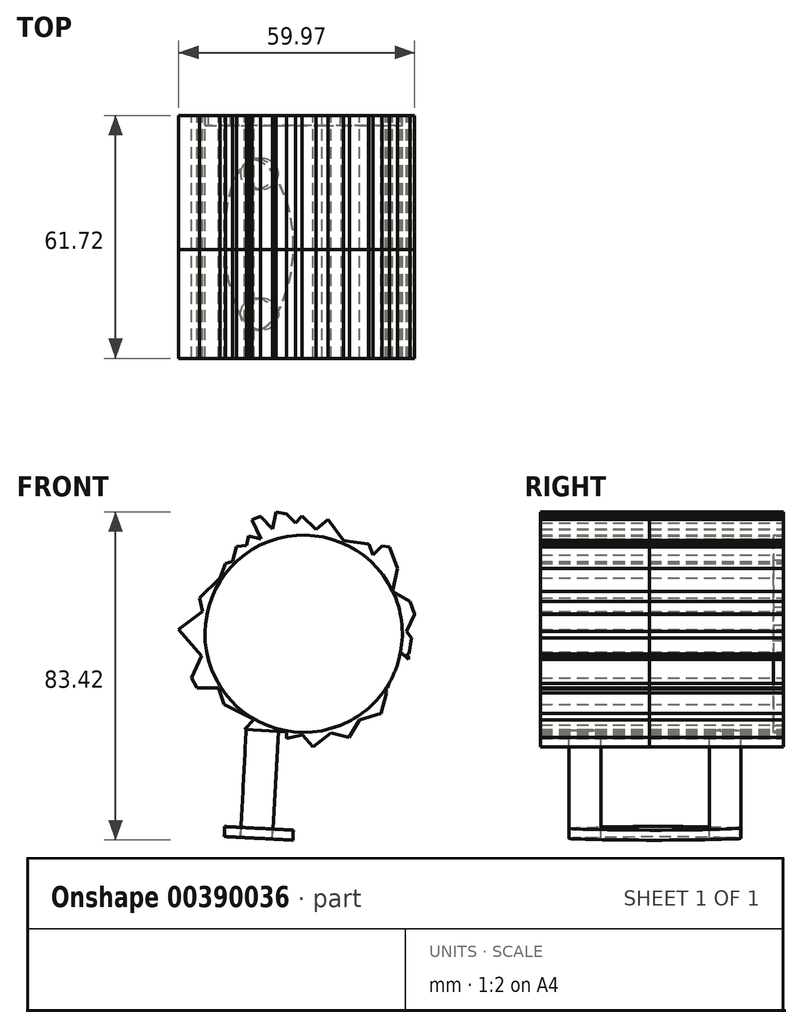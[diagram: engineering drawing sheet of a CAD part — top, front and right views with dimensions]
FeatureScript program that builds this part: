
annotation { "Feature Type Name" : "Feature", "Feature Type Description" : "" }
export const myFeature = defineFeature(function(context is Context, id is Id, definition is map)
    precondition{}
    {
        {
            var Q0;
            Q0=qCreatedBy(makeId("Front.planeOp"),FACE);
            var sketch = newSketch(context, id + "F0", { "sketchPlane" : qUnion([Q0])});
            skCircle(sketch, "E0", {"center": v(0, 0) * mm, "radius": 31.78 * mm});
            skCircle(sketch, "E1", {"center": v(0, 0) * mm, "radius": 25.06 * mm});
            skLineSegment(sketch, "E2", {"start": v(28.67, -13.71) * mm, "end": v(22.7, -10.64) * mm});
            skLineSegment(sketch, "E3", {"start": v(22.7, -10.64) * mm, "end": v(28.67, -13.71) * mm});
            skLineSegment(sketch, "E4", {"start": v(24.63, -4.65) * mm, "end": v(31.2, -6.06) * mm});
            skLineSegment(sketch, "E5", {"start": v(31.2, -6.06) * mm, "end": v(24.98, 2.05) * mm});
            skLineSegment(sketch, "E6", {"start": v(24.98, 2.05) * mm, "end": v(31.27, 5.68) * mm});
            skLineSegment(sketch, "E7", {"start": v(31.27, 5.68) * mm, "end": v(22.62, 10.8) * mm});
            skLineSegment(sketch, "E8", {"start": v(22.62, 10.8) * mm, "end": v(24.6, 20.1) * mm});
            skLineSegment(sketch, "E9", {"start": v(24.6, 20.1) * mm, "end": v(31.56, -3.73) * mm});
            skLineSegment(sketch, "E10", {"start": v(31.56, -3.73) * mm, "end": v(21.15, 23.72) * mm});
            skLineSegment(sketch, "E11", {"start": v(21.15, 23.72) * mm, "end": v(16.52, 18.85) * mm});
            skLineSegment(sketch, "E12", {"start": v(16.52, 18.85) * mm, "end": v(16.52, 27.15) * mm});
            skLineSegment(sketch, "E13", {"start": v(16.52, 27.15) * mm, "end": v(12.53, 21.7) * mm});
            skLineSegment(sketch, "E14", {"start": v(12.53, 21.7) * mm, "end": v(21.15, 23.72) * mm});
            skLineSegment(sketch, "E15", {"start": v(12.53, 21.7) * mm, "end": v(8.2, 30.7) * mm});
            skLineSegment(sketch, "E16", {"start": v(8.2, 30.7) * mm, "end": v(1.3, 25.03) * mm});
            skLineSegment(sketch, "E17", {"start": v(1.3, 25.03) * mm, "end": v(-4.38, 30.44) * mm});
            skLineSegment(sketch, "E18", {"start": v(-4.38, 30.44) * mm, "end": v(-5.66, 24.42) * mm});
            skLineSegment(sketch, "E19", {"start": v(-5.66, 24.42) * mm, "end": v(1.32, 31.75) * mm});
            skLineSegment(sketch, "E20", {"start": v(1.32, 31.75) * mm, "end": v(-4.38, 30.44) * mm});
            skLineSegment(sketch, "E21", {"start": v(-4.38, 30.44) * mm, "end": v(-7, 31) * mm});
            skLineSegment(sketch, "E22", {"start": v(-7, 31) * mm, "end": v(-8.58, 23.55) * mm});
            skLineSegment(sketch, "E23", {"start": v(-8.58, 23.55) * mm, "end": v(-18.38, 25.93) * mm});
            skLineSegment(sketch, "E24", {"start": v(-18.38, 25.93) * mm, "end": v(-15, 20.08) * mm});
            skLineSegment(sketch, "E25", {"start": v(-15, 20.08) * mm, "end": v(-13.1, 28.95) * mm});
            skLineSegment(sketch, "E26", {"start": v(-13.1, 28.95) * mm, "end": v(-10.3, 22.85) * mm});
            skLineSegment(sketch, "E27", {"start": v(-10.3, 22.85) * mm, "end": v(-23.2, 21.7) * mm});
            skLineSegment(sketch, "E28", {"start": v(-23.2, 21.7) * mm, "end": v(-18.34, 17.08) * mm});
            skLineSegment(sketch, "E29", {"start": v(-18.34, 17.08) * mm, "end": v(-15.8, 27.57) * mm});
            skLineSegment(sketch, "E30", {"start": v(-15.8, 27.57) * mm, "end": v(-23.2, 9.5) * mm});
            skLineSegment(sketch, "E31", {"start": v(-23.2, 9.5) * mm, "end": v(-26.44, 17.63) * mm});
            skLineSegment(sketch, "E32", {"start": v(-26.44, 17.63) * mm, "end": v(-20.07, 15.02) * mm});
            skLineSegment(sketch, "E33", {"start": v(-20.07, 15.02) * mm, "end": v(-29.9, 10.78) * mm});
            skLineSegment(sketch, "E34", {"start": v(-29.9, 10.78) * mm, "end": v(-24.96, 2.24) * mm});
            skLineSegment(sketch, "E35", {"start": v(-24.96, 2.24) * mm, "end": v(-27.74, 15.5) * mm});
            skLineSegment(sketch, "E36", {"start": v(-27.74, 15.5) * mm, "end": v(-16.65, 18.74) * mm});
            skLineSegment(sketch, "E37", {"start": v(-16.65, 18.74) * mm, "end": v(-31.52, 4.06) * mm});
            skLineSegment(sketch, "E38", {"start": v(-31.52, 4.06) * mm, "end": v(-25.05, -0.69) * mm});
            skLineSegment(sketch, "E39", {"start": v(-25.05, -0.69) * mm, "end": v(-31.58, -3.5) * mm});
            skLineSegment(sketch, "E40", {"start": v(-31.58, -3.5) * mm, "end": v(-23.73, -8.07) * mm});
            skLineSegment(sketch, "E41", {"start": v(-23.73, -8.07) * mm, "end": v(-31.76, 1.15) * mm});
            skLineSegment(sketch, "E42", {"start": v(-31.76, 1.15) * mm, "end": v(-24.13, 6.78) * mm});
            skLineSegment(sketch, "E43", {"start": v(-24.13, 6.78) * mm, "end": v(-24.96, 2.24) * mm});
            skLineSegment(sketch, "E44", {"start": v(-24.84, -3.3) * mm, "end": v(-29.17, -12.6) * mm});
            skLineSegment(sketch, "E45", {"start": v(-29.17, -12.6) * mm, "end": v(-22.66, -10.7) * mm});
            skLineSegment(sketch, "E46", {"start": v(-22.66, -10.7) * mm, "end": v(-31.1, -6.5) * mm});
            skLineSegment(sketch, "E47", {"start": v(-31.1, -6.5) * mm, "end": v(-21.95, -22.98) * mm});
            skLineSegment(sketch, "E48", {"start": v(-21.95, -22.98) * mm, "end": v(-20.98, -13.71) * mm});
            skLineSegment(sketch, "E49", {"start": v(-20.98, -13.71) * mm, "end": v(-28.67, -13.71) * mm});
            skLineSegment(sketch, "E50", {"start": v(-28.67, -13.71) * mm, "end": v(-12.57, -21.74) * mm});
            skLineSegment(sketch, "E51", {"start": v(-12.57, -21.74) * mm, "end": v(-17.27, -26.67) * mm});
            skLineSegment(sketch, "E52", {"start": v(-17.27, -26.67) * mm, "end": v(-22.66, -10.7) * mm});
            skLineSegment(sketch, "E53", {"start": v(-22.66, -10.7) * mm, "end": v(-20.83, -24) * mm});
            skLineSegment(sketch, "E54", {"start": v(-20.83, -24) * mm, "end": v(-4.38, -24.87) * mm});
            skLineSegment(sketch, "E55", {"start": v(-4.38, -24.87) * mm, "end": v(-4.38, -31.47) * mm});
            skLineSegment(sketch, "E56", {"start": v(-4.38, -31.47) * mm, "end": v(-10.3, -22.85) * mm});
            skLineSegment(sketch, "E57", {"start": v(-10.3, -22.85) * mm, "end": v(-13.69, -28.68) * mm});
            skLineSegment(sketch, "E58", {"start": v(-13.69, -28.68) * mm, "end": v(4.1, -24.73) * mm});
            skLineSegment(sketch, "E59", {"start": v(4.1, -24.73) * mm, "end": v(4.74, -31.42) * mm});
            skLineSegment(sketch, "E60", {"start": v(4.74, -31.42) * mm, "end": v(-0.8, -25.05) * mm});
            skLineSegment(sketch, "E61", {"start": v(-0.8, -25.05) * mm, "end": v(-1.35, -31.75) * mm});
            skLineSegment(sketch, "E62", {"start": v(-1.35, -31.75) * mm, "end": v(9.56, -23.17) * mm});
            skLineSegment(sketch, "E63", {"start": v(9.56, -23.17) * mm, "end": v(21.75, -23.17) * mm});
            skLineSegment(sketch, "E64", {"start": v(21.75, -23.17) * mm, "end": v(9.17, -30.42) * mm});
            skLineSegment(sketch, "E65", {"start": v(9.17, -30.42) * mm, "end": v(15.34, -19.82) * mm});
            skLineSegment(sketch, "E66", {"start": v(15.34, -19.82) * mm, "end": v(16.07, -27.41) * mm});
            skLineSegment(sketch, "E67", {"start": v(16.07, -27.41) * mm, "end": v(4.62, -24.63) * mm});
            skLineSegment(sketch, "E68", {"start": v(4.62, -24.63) * mm, "end": v(25.88, -18.44) * mm});
            skLineSegment(sketch, "E69", {"start": v(25.88, -18.44) * mm, "end": v(24.63, -4.65) * mm});
            skLineSegment(sketch, "E70", {"start": v(24.63, -4.65) * mm, "end": v(30.18, -9.94) * mm});
            skLineSegment(sketch, "E71", {"start": v(30.18, -9.94) * mm, "end": v(20.8, -13.98) * mm});
            skLineSegment(sketch, "E72", {"start": v(20.8, -13.98) * mm, "end": v(22.7, -22.24) * mm});
            skLineSegment(sketch, "E73", {"start": v(22.7, -22.24) * mm, "end": v(17.22, -18.21) * mm});
            skLineSegment(sketch, "E74", {"start": v(17.22, -18.21) * mm, "end": v(17.99, -26.2) * mm});
            skLineSegment(sketch, "E75", {"start": v(17.99, -26.2) * mm, "end": v(21.66, -12.6) * mm});
            skLineSegment(sketch, "E76", {"start": v(21.66, -12.6) * mm, "end": v(24.8, -19.88) * mm});
            skLineSegment(sketch, "E77", {"start": v(24.8, -19.88) * mm, "end": v(29.22, 12.48) * mm});
            skLineSegment(sketch, "E78", {"start": v(29.22, 12.48) * mm, "end": v(31.56, -4.65) * mm});
            skLineSegment(sketch, "E79", {"start": v(31.56, -4.65) * mm, "end": v(29.17, -12.6) * mm});
            skLineSegment(sketch, "E80", {"start": v(29.17, -12.6) * mm, "end": v(24.98, -1.56) * mm});
            skLineSegment(sketch, "E81", {"start": v(24.98, -1.56) * mm, "end": v(30.18, 8.9) * mm});
            skLineSegment(sketch, "E82", {"start": v(30.18, 8.9) * mm, "end": v(24.17, 6.62) * mm});
            skLineSegment(sketch, "E83", {"start": v(24.17, 6.62) * mm, "end": v(26.74, 17.18) * mm});
            skLineSegment(sketch, "E84", {"start": v(26.74, 17.18) * mm, "end": v(18.93, 16.43) * mm});
            skLineSegment(sketch, "E85", {"start": v(18.93, 16.43) * mm, "end": v(22.98, 21.95) * mm});
            skLineSegment(sketch, "E86", {"start": v(22.98, 21.95) * mm, "end": v(6.53, 24.2) * mm});
            skLineSegment(sketch, "E87", {"start": v(6.53, 24.2) * mm, "end": v(12.36, 29.28) * mm});
            skLineSegment(sketch, "E88", {"start": v(12.36, 29.28) * mm, "end": v(-0.35, 30) * mm});
            skLineSegment(sketch, "E89", {"start": v(-0.35, 30) * mm, "end": v(5.02, 24.56) * mm});
            skLineSegment(sketch, "E90", {"start": v(5.02, 24.56) * mm, "end": v(4.3, 31.49) * mm});
            skLineSegment(sketch, "E91", {"start": v(4.3, 31.49) * mm, "end": v(11.09, 22.48) * mm});
            skLineSegment(sketch, "E92", {"start": v(11.09, 22.48) * mm, "end": v(14.54, 28.26) * mm});
            skLineSegment(sketch, "E93", {"start": v(14.54, 28.26) * mm, "end": v(18.93, 16.43) * mm});
            skLineSegment(sketch, "E94", {"start": v(-11, 29.82) * mm, "end": v(-5.66, 24.42) * mm});
            skSolve(sketch);
        }
        {
            var Q0;
            {var subQ0=sQuery(id+"F0.wireOp",EDGE,"E94");var subQ3=sQuery(id+"F0.wireOp",EDGE,"E22");var subQ5=makeQuery(id+"F0.imprint","INTERSECT",VERTEX,{"derivedFrom":[subQ3,subQ0]});Q0=makeQuery(id+"F0.imprint","IMPRINT",FACE,{"disambiguationData":[TD([[makeQuery(id+"F0.imprint","IMPRINT",EDGE,{"disambiguationData":[TD([[subQ5,-1.0]])],"derivedFrom":subQ3}),1.0]])]});}
            var Q1;
            {var subQ0=sQuery(id+"F0.wireOp",EDGE,"E17");var subQ3=sQuery(id+"F0.wireOp",EDGE,"E19");var subQ5=makeQuery(id+"F0.imprint","INTERSECT",VERTEX,{"derivedFrom":[subQ0,subQ3]});Q1=makeQuery(id+"F0.imprint","IMPRINT",FACE,{"disambiguationData":[TD([[makeQuery(id+"F0.imprint","IMPRINT",EDGE,{"disambiguationData":[TD([[subQ5,1.0]])],"derivedFrom":subQ0}),1.0]])]});}
            var Q2;
            {var subQ0=sQuery(id+"F0.wireOp",EDGE,"E16");var subQ3=sQuery(id+"F0.wireOp",EDGE,"E89");var subQ5=makeQuery(id+"F0.imprint","INTERSECT",VERTEX,{"derivedFrom":[subQ0,subQ3]});Q2=makeQuery(id+"F0.imprint","IMPRINT",FACE,{"disambiguationData":[TD([[makeQuery(id+"F0.imprint","IMPRINT",EDGE,{"disambiguationData":[TD([[subQ5,-1.0]])],"derivedFrom":subQ0}),1.0]])]});}
            var Q3;
            {var subQ0=sQuery(id+"F0.wireOp",EDGE,"E86");var subQ3=sQuery(id+"F0.wireOp",EDGE,"E91");var subQ5=makeQuery(id+"F0.imprint","INTERSECT",VERTEX,{"derivedFrom":[subQ0,subQ3]});Q3=makeQuery(id+"F0.imprint","IMPRINT",FACE,{"disambiguationData":[TD([[makeQuery(id+"F0.imprint","IMPRINT",EDGE,{"disambiguationData":[TD([[subQ5,-1.0]])],"derivedFrom":subQ0}),1.0]])]});}
            var Q4;
            {var subQ3=sQuery(id+"F0.wireOp",EDGE,"E16");var subQ7=sQuery(id+"F0.wireOp",EDGE,"E91");var subQ9=makeQuery(id+"F0.imprint","INTERSECT",VERTEX,{"derivedFrom":[subQ3,subQ7]});Q4=makeQuery(id+"F0.imprint","IMPRINT",FACE,{"disambiguationData":[TD([[makeQuery(id+"F0.imprint","IMPRINT",EDGE,{"disambiguationData":[TD([[subQ9,-1.0]])],"derivedFrom":subQ3}),1.0]])]});}
            var Q5;
            {var subQ0=sQuery(id+"F0.wireOp",EDGE,"E15");var subQ3=sQuery(id+"F0.wireOp",EDGE,"E92");var subQ5=makeQuery(id+"F0.imprint","INTERSECT",VERTEX,{"derivedFrom":[subQ0,subQ3]});Q5=makeQuery(id+"F0.imprint","IMPRINT",FACE,{"disambiguationData":[TD([[makeQuery(id+"F0.imprint","IMPRINT",EDGE,{"disambiguationData":[TD([[subQ5,1.0]])],"derivedFrom":subQ3}),-1.0]])]});}
            var Q6;
            {var subQ0=sQuery(id+"F0.wireOp",EDGE,"E92");var subQ1=sQuery(id+"F0.wireOp",EDGE,"E15");var subQ2=makeQuery(id+"F0.imprint","INTERSECT",VERTEX,{"derivedFrom":[subQ1,subQ0]});Q6=makeQuery(id+"F0.imprint","IMPRINT",FACE,{"disambiguationData":[TD([[makeQuery(id+"F0.imprint","IMPRINT",EDGE,{"disambiguationData":[TD([[subQ2,-1.0]])],"derivedFrom":subQ1}),1.0]])]});}
            var Q7;
            {var subQ0=sQuery(id+"F0.wireOp",EDGE,"E12");var subQ3=sQuery(id+"F0.wireOp",EDGE,"E14");var subQ5=makeQuery(id+"F0.imprint","INTERSECT",VERTEX,{"derivedFrom":[subQ0,subQ3]});Q7=makeQuery(id+"F0.imprint","IMPRINT",FACE,{"disambiguationData":[TD([[makeQuery(id+"F0.imprint","IMPRINT",EDGE,{"disambiguationData":[TD([[subQ5,1.0]])],"derivedFrom":subQ0}),1.0]])]});}
            var Q8;
            {var subQ0=sQuery(id+"F0.wireOp",EDGE,"E11");var subQ3=sQuery(id+"F0.wireOp",EDGE,"E93");var subQ5=makeQuery(id+"F0.imprint","INTERSECT",VERTEX,{"derivedFrom":[subQ0,subQ3]});Q8=makeQuery(id+"F0.imprint","IMPRINT",FACE,{"disambiguationData":[TD([[makeQuery(id+"F0.imprint","IMPRINT",EDGE,{"disambiguationData":[TD([[subQ5,-1.0]])],"derivedFrom":subQ0}),1.0]])]});}
            var Q9;
            {var subQ0=sQuery(id+"F0.wireOp",EDGE,"E8");var subQ5=sQuery(id+"F0.wireOp",EDGE,"E10");var subQ6=makeQuery(id+"F0.imprint","INTERSECT",VERTEX,{"derivedFrom":[subQ0,subQ5]});Q9=makeQuery(id+"F0.imprint","IMPRINT",FACE,{"disambiguationData":[TD([[makeQuery(id+"F0.imprint","IMPRINT",EDGE,{"disambiguationData":[TD([[subQ6,-1.0]])],"derivedFrom":subQ5}),1.0]])]});}
            var Q10;
            {var subQ0=sQuery(id+"F0.wireOp",EDGE,"E7");var subQ3=sQuery(id+"F0.wireOp",EDGE,"E83");var subQ5=makeQuery(id+"F0.imprint","INTERSECT",VERTEX,{"derivedFrom":[subQ0,subQ3]});Q10=makeQuery(id+"F0.imprint","IMPRINT",FACE,{"disambiguationData":[TD([[makeQuery(id+"F0.imprint","IMPRINT",EDGE,{"disambiguationData":[TD([[subQ5,-1.0]])],"derivedFrom":subQ0}),1.0]])]});}
            var Q11;
            {var subQ0=sQuery(id+"F0.wireOp",EDGE,"E77");var subQ1=sQuery(id+"F0.wireOp",EDGE,"E10");var subQ2=makeQuery(id+"F0.imprint","INTERSECT",VERTEX,{"derivedFrom":[subQ1,subQ0]});Q11=makeQuery(id+"F0.imprint","IMPRINT",FACE,{"disambiguationData":[TD([[makeQuery(id+"F0.imprint","IMPRINT",EDGE,{"disambiguationData":[TD([[subQ2,-1.0]])],"derivedFrom":subQ1}),1.0]])]});}
            var Q12;
            {var subQ1=sQuery(id+"F0.wireOp",EDGE,"E1");var subQ3=sQuery(id+"F0.wireOp",EDGE,"E81");var subQ4=makeQuery(id+"F0.imprint","INTERSECT",VERTEX,{"derivedFrom":[subQ1,subQ3]});Q12=makeQuery(id+"F0.imprint","IMPRINT",FACE,{"disambiguationData":[TD([[makeQuery(id+"F0.imprint","IMPRINT",EDGE,{"disambiguationData":[TD([[subQ4,-1.0]])],"derivedFrom":subQ3}),1.0]])]});}
            var Q13;
            {var subQ1=sQuery(id+"F0.wireOp",EDGE,"E1");var subQ3=sQuery(id+"F0.wireOp",EDGE,"E80");var subQ4=makeQuery(id+"F0.imprint","INTERSECT",VERTEX,{"derivedFrom":[subQ1,subQ3]});Q13=makeQuery(id+"F0.imprint","IMPRINT",FACE,{"disambiguationData":[TD([[makeQuery(id+"F0.imprint","IMPRINT",EDGE,{"disambiguationData":[TD([[subQ4,1.0]])],"derivedFrom":subQ3}),1.0]])]});}
            var Q14;
            {var subQ0=sQuery(id+"F0.wireOp",EDGE,"E3");var subQ1=sQuery(id+"F0.wireOp",EDGE,"E1");var subQ2=makeQuery(id+"F0.imprint","INTERSECT",VERTEX,{"derivedFrom":[subQ1,subQ0]});Q14=makeQuery(id+"F0.imprint","IMPRINT",FACE,{"disambiguationData":[TD([[makeQuery(id+"F0.imprint","IMPRINT",EDGE,{"disambiguationData":[TD([[subQ2,-1.0]])],"derivedFrom":subQ0}),1.0]])]});}
            var Q15;
            {var subQ0=sQuery(id+"F0.wireOp",EDGE,"E71");var subQ3=sQuery(id+"F0.wireOp",EDGE,"E75");var subQ5=makeQuery(id+"F0.imprint","INTERSECT",VERTEX,{"derivedFrom":[subQ0,subQ3]});Q15=makeQuery(id+"F0.imprint","IMPRINT",FACE,{"disambiguationData":[TD([[makeQuery(id+"F0.imprint","IMPRINT",EDGE,{"disambiguationData":[TD([[subQ5,-1.0]])],"derivedFrom":subQ0}),-1.0]])]});}
            var Q16;
            {var subQ0=sQuery(id+"F0.wireOp",EDGE,"E72");var subQ5=sQuery(id+"F0.wireOp",EDGE,"E75");var subQ6=makeQuery(id+"F0.imprint","INTERSECT",VERTEX,{"derivedFrom":[subQ0,subQ5]});Q16=makeQuery(id+"F0.imprint","IMPRINT",FACE,{"disambiguationData":[TD([[makeQuery(id+"F0.imprint","IMPRINT",EDGE,{"disambiguationData":[TD([[subQ6,1.0]])],"derivedFrom":subQ5}),1.0]])]});}
            var Q17;
            {var subQ5=sQuery(id+"F0.wireOp",EDGE,"E3");var subQ7=sQuery(id+"F0.wireOp",EDGE,"E1");var subQ8=makeQuery(id+"F0.imprint","INTERSECT",VERTEX,{"derivedFrom":[subQ7,subQ5]});Q17=makeQuery(id+"F0.imprint","IMPRINT",FACE,{"disambiguationData":[TD([[makeQuery(id+"F0.imprint","IMPRINT",EDGE,{"disambiguationData":[TD([[subQ8,-1.0]])],"derivedFrom":subQ5}),-1.0]])]});}
            var Q18;
            {var subQ0=sQuery(id+"F0.wireOp",EDGE,"E66");var subQ5=sQuery(id+"F0.wireOp",EDGE,"E68");var subQ7=makeQuery(id+"F0.imprint","INTERSECT",VERTEX,{"derivedFrom":[subQ0,subQ5]});Q18=makeQuery(id+"F0.imprint","IMPRINT",FACE,{"disambiguationData":[TD([[makeQuery(id+"F0.imprint","IMPRINT",EDGE,{"disambiguationData":[TD([[subQ7,-1.0]])],"derivedFrom":subQ5}),1.0]])]});}
            var Q19;
            {var subQ0=sQuery(id+"F0.wireOp",EDGE,"E63");var subQ5=sQuery(id+"F0.wireOp",EDGE,"E68");var subQ6=makeQuery(id+"F0.imprint","INTERSECT",VERTEX,{"derivedFrom":[subQ0,subQ5]});Q19=makeQuery(id+"F0.imprint","IMPRINT",FACE,{"disambiguationData":[TD([[makeQuery(id+"F0.imprint","IMPRINT",EDGE,{"disambiguationData":[TD([[subQ6,-1.0]])],"derivedFrom":subQ5}),1.0]])]});}
            var Q20;
            {var subQ0=sQuery(id+"F0.wireOp",EDGE,"E58");var subQ3=sQuery(id+"F0.wireOp",EDGE,"E60");var subQ5=makeQuery(id+"F0.imprint","INTERSECT",VERTEX,{"derivedFrom":[subQ0,subQ3]});Q20=makeQuery(id+"F0.imprint","IMPRINT",FACE,{"disambiguationData":[TD([[makeQuery(id+"F0.imprint","IMPRINT",EDGE,{"disambiguationData":[TD([[subQ5,-1.0]])],"derivedFrom":subQ0}),1.0]])]});}
            var Q21;
            {var subQ3=sQuery(id+"F0.wireOp",EDGE,"E54");var subQ5=sQuery(id+"F0.wireOp",EDGE,"E55");var subQ6=makeQuery(id+"F0.imprint","INTERSECT",VERTEX,{"derivedFrom":[subQ3,subQ5]});Q21=makeQuery(id+"F0.imprint","IMPRINT",FACE,{"disambiguationData":[TD([[makeQuery(id+"F0.imprint","IMPRINT",EDGE,{"disambiguationData":[TD([[subQ6,1.0]])],"derivedFrom":subQ3}),1.0]])]});}
            var Q22;
            {var subQ0=sQuery(id+"F0.wireOp",EDGE,"E61");var subQ1=sQuery(id+"F0.wireOp",EDGE,"E58");var subQ2=makeQuery(id+"F0.imprint","INTERSECT",VERTEX,{"derivedFrom":[subQ1,subQ0]});Q22=makeQuery(id+"F0.imprint","IMPRINT",FACE,{"disambiguationData":[TD([[makeQuery(id+"F0.imprint","IMPRINT",EDGE,{"disambiguationData":[TD([[subQ2,-1.0]])],"derivedFrom":subQ1}),1.0]])]});}
            var Q23;
            {var subQ0=sQuery(id+"F0.wireOp",EDGE,"E51");var subQ1=sQuery(id+"F0.wireOp",EDGE,"E50");var subQ2=makeQuery(id+"F0.imprint","INTERSECT",VERTEX,{"derivedFrom":[subQ1,subQ0]});Q23=makeQuery(id+"F0.imprint","IMPRINT",FACE,{"disambiguationData":[TD([[makeQuery(id+"F0.imprint","IMPRINT",EDGE,{"disambiguationData":[TD([[subQ2,1.0]])],"derivedFrom":subQ1}),1.0]])]});}
            var Q24;
            {var subQ1=sQuery(id+"F0.wireOp",EDGE,"E48");var subQ3=sQuery(id+"F0.wireOp",EDGE,"E52");var subQ4=makeQuery(id+"F0.imprint","INTERSECT",VERTEX,{"derivedFrom":[subQ1,subQ3]});Q24=makeQuery(id+"F0.imprint","IMPRINT",FACE,{"disambiguationData":[TD([[makeQuery(id+"F0.imprint","IMPRINT",EDGE,{"disambiguationData":[TD([[subQ4,-1.0]])],"derivedFrom":subQ3}),-1.0]])]});}
            var Q25;
            {var subQ0=sQuery(id+"F0.wireOp",EDGE,"E52");var subQ3=sQuery(id+"F0.wireOp",EDGE,"E49");var subQ5=makeQuery(id+"F0.imprint","INTERSECT",VERTEX,{"derivedFrom":[subQ3,subQ0]});Q25=makeQuery(id+"F0.imprint","IMPRINT",FACE,{"disambiguationData":[TD([[makeQuery(id+"F0.imprint","IMPRINT",EDGE,{"disambiguationData":[TD([[subQ5,1.0]])],"derivedFrom":subQ3}),-1.0]])]});}
            var Q26;
            {var subQ0=sQuery(id+"F0.wireOp",EDGE,"E40");var subQ5=sQuery(id+"F0.wireOp",EDGE,"E44");var subQ6=makeQuery(id+"F0.imprint","INTERSECT",VERTEX,{"derivedFrom":[subQ0,subQ5]});Q26=makeQuery(id+"F0.imprint","IMPRINT",FACE,{"disambiguationData":[TD([[makeQuery(id+"F0.imprint","IMPRINT",EDGE,{"disambiguationData":[TD([[subQ6,-1.0]])],"derivedFrom":subQ5}),1.0]])]});}
            var Q27;
            {var subQ1=sQuery(id+"F0.wireOp",EDGE,"E1");var subQ3=sQuery(id+"F0.wireOp",EDGE,"E44");var subQ4=makeQuery(id+"F0.imprint","INTERSECT",VERTEX,{"derivedFrom":[subQ1,subQ3]});Q27=makeQuery(id+"F0.imprint","IMPRINT",FACE,{"disambiguationData":[TD([[makeQuery(id+"F0.imprint","IMPRINT",EDGE,{"disambiguationData":[TD([[subQ4,-1.0]])],"derivedFrom":subQ3}),1.0]])]});}
            var Q28;
            {var subQ1=sQuery(id+"F0.wireOp",EDGE,"E40");var subQ3=sQuery(id+"F0.wireOp",EDGE,"E44");var subQ4=makeQuery(id+"F0.imprint","INTERSECT",VERTEX,{"derivedFrom":[subQ1,subQ3]});Q28=makeQuery(id+"F0.imprint","IMPRINT",FACE,{"disambiguationData":[TD([[makeQuery(id+"F0.imprint","IMPRINT",EDGE,{"disambiguationData":[TD([[subQ4,1.0]])],"derivedFrom":subQ3}),1.0]])]});}
            var Q29;
            {var subQ0=sQuery(id+"F0.wireOp",EDGE,"E39");var subQ5=sQuery(id+"F0.wireOp",EDGE,"E41");var subQ6=makeQuery(id+"F0.imprint","INTERSECT",VERTEX,{"derivedFrom":[subQ0,subQ5]});Q29=makeQuery(id+"F0.imprint","IMPRINT",FACE,{"disambiguationData":[TD([[makeQuery(id+"F0.imprint","IMPRINT",EDGE,{"disambiguationData":[TD([[subQ6,1.0]])],"derivedFrom":subQ5}),-1.0]])]});}
            var Q30;
            {var subQ0=sQuery(id+"F0.wireOp",EDGE,"E34");var subQ5=sQuery(id+"F0.wireOp",EDGE,"E42");var subQ6=makeQuery(id+"F0.imprint","INTERSECT",VERTEX,{"derivedFrom":[subQ0,subQ5]});Q30=makeQuery(id+"F0.imprint","IMPRINT",FACE,{"disambiguationData":[TD([[makeQuery(id+"F0.imprint","IMPRINT",EDGE,{"disambiguationData":[TD([[subQ6,1.0]])],"derivedFrom":subQ5}),-1.0]])]});}
            var Q31;
            {var subQ1=sQuery(id+"F0.wireOp",EDGE,"E35");var subQ4=sQuery(id+"F0.wireOp",EDGE,"E42");var subQ6=makeQuery(id+"F0.imprint","INTERSECT",VERTEX,{"derivedFrom":[subQ1,subQ4]});Q31=makeQuery(id+"F0.imprint","IMPRINT",FACE,{"disambiguationData":[TD([[makeQuery(id+"F0.imprint","IMPRINT",EDGE,{"disambiguationData":[TD([[subQ6,-1.0]])],"derivedFrom":subQ4}),-1.0]])]});}
            var Q32;
            {var subQ3=sQuery(id+"F0.wireOp",EDGE,"E35");var subQ5=sQuery(id+"F0.wireOp",EDGE,"E42");var subQ6=makeQuery(id+"F0.imprint","INTERSECT",VERTEX,{"derivedFrom":[subQ3,subQ5]});Q32=makeQuery(id+"F0.imprint","IMPRINT",FACE,{"disambiguationData":[TD([[makeQuery(id+"F0.imprint","IMPRINT",EDGE,{"disambiguationData":[TD([[subQ6,-1.0]])],"derivedFrom":subQ3}),-1.0]])]});}
            var Q33;
            {var subQ1=sQuery(id+"F0.wireOp",EDGE,"E30");var subQ3=sQuery(id+"F0.wireOp",EDGE,"E37");var subQ4=makeQuery(id+"F0.imprint","INTERSECT",VERTEX,{"derivedFrom":[subQ1,subQ3]});Q33=makeQuery(id+"F0.imprint","IMPRINT",FACE,{"disambiguationData":[TD([[makeQuery(id+"F0.imprint","IMPRINT",EDGE,{"disambiguationData":[TD([[subQ4,-1.0]])],"derivedFrom":subQ3}),1.0]])]});}
            var Q34;
            {var subQ1=sQuery(id+"F0.wireOp",EDGE,"E32");var subQ3=sQuery(id+"F0.wireOp",EDGE,"E37");var subQ4=makeQuery(id+"F0.imprint","INTERSECT",VERTEX,{"derivedFrom":[subQ1,subQ3]});Q34=makeQuery(id+"F0.imprint","IMPRINT",FACE,{"disambiguationData":[TD([[makeQuery(id+"F0.imprint","IMPRINT",EDGE,{"disambiguationData":[TD([[subQ4,-1.0]])],"derivedFrom":subQ3}),1.0]])]});}
            var Q35;
            {var subQ1=sQuery(id+"F0.wireOp",EDGE,"E1");var subQ3=sQuery(id+"F0.wireOp",EDGE,"E37");var subQ4=makeQuery(id+"F0.imprint","INTERSECT",VERTEX,{"derivedFrom":[subQ1,subQ3]});Q35=makeQuery(id+"F0.imprint","IMPRINT",FACE,{"disambiguationData":[TD([[makeQuery(id+"F0.imprint","IMPRINT",EDGE,{"disambiguationData":[TD([[subQ4,-1.0]])],"derivedFrom":subQ3}),1.0]])]});}
            var Q36;
            {var subQ1=sQuery(id+"F0.wireOp",EDGE,"E30");var subQ5=sQuery(id+"F0.wireOp",EDGE,"E36");var subQ6=makeQuery(id+"F0.imprint","INTERSECT",VERTEX,{"derivedFrom":[subQ1,subQ5]});Q36=makeQuery(id+"F0.imprint","IMPRINT",FACE,{"disambiguationData":[TD([[makeQuery(id+"F0.imprint","IMPRINT",EDGE,{"disambiguationData":[TD([[subQ6,-1.0]])],"derivedFrom":subQ1}),1.0]])]});}
            var Q37;
            {var subQ0=sQuery(id+"F0.wireOp",EDGE,"E32");var subQ1=sQuery(id+"F0.wireOp",EDGE,"E30");var subQ2=makeQuery(id+"F0.imprint","INTERSECT",VERTEX,{"derivedFrom":[subQ1,subQ0]});Q37=makeQuery(id+"F0.imprint","IMPRINT",FACE,{"disambiguationData":[TD([[makeQuery(id+"F0.imprint","IMPRINT",EDGE,{"disambiguationData":[TD([[subQ2,-1.0]])],"derivedFrom":subQ1}),1.0]])]});}
            var Q38;
            {var subQ1=sQuery(id+"F0.wireOp",EDGE,"E28");var subQ3=sQuery(id+"F0.wireOp",EDGE,"E36");var subQ4=makeQuery(id+"F0.imprint","INTERSECT",VERTEX,{"derivedFrom":[subQ1,subQ3]});Q38=makeQuery(id+"F0.imprint","IMPRINT",FACE,{"disambiguationData":[TD([[makeQuery(id+"F0.imprint","IMPRINT",EDGE,{"disambiguationData":[TD([[subQ4,-1.0]])],"derivedFrom":subQ3}),-1.0]])]});}
            var Q39;
            {var subQ0=sQuery(id+"F0.wireOp",EDGE,"E33");var subQ1=sQuery(id+"F0.wireOp",EDGE,"E30");var subQ2=makeQuery(id+"F0.imprint","INTERSECT",VERTEX,{"derivedFrom":[subQ1,subQ0]});Q39=makeQuery(id+"F0.imprint","IMPRINT",FACE,{"disambiguationData":[TD([[makeQuery(id+"F0.imprint","IMPRINT",EDGE,{"disambiguationData":[TD([[subQ2,-1.0]])],"derivedFrom":subQ1}),1.0]])]});}
            var Q40;
            {var subQ0=sQuery(id+"F0.wireOp",EDGE,"E30");var subQ5=sQuery(id+"F0.wireOp",EDGE,"E37");var subQ6=makeQuery(id+"F0.imprint","INTERSECT",VERTEX,{"derivedFrom":[subQ0,subQ5]});Q40=makeQuery(id+"F0.imprint","IMPRINT",FACE,{"disambiguationData":[TD([[makeQuery(id+"F0.imprint","IMPRINT",EDGE,{"disambiguationData":[TD([[subQ6,1.0]])],"derivedFrom":subQ5}),1.0]])]});}
            var Q41;
            {var subQ0=sQuery(id+"F0.wireOp",EDGE,"E29");var subQ3=sQuery(id+"F0.wireOp",EDGE,"E36");var subQ5=makeQuery(id+"F0.imprint","INTERSECT",VERTEX,{"derivedFrom":[subQ0,subQ3]});Q41=makeQuery(id+"F0.imprint","IMPRINT",FACE,{"disambiguationData":[TD([[makeQuery(id+"F0.imprint","IMPRINT",EDGE,{"disambiguationData":[TD([[subQ5,1.0]])],"derivedFrom":subQ0}),-1.0]])]});}
            var Q42;
            {var subQ0=sQuery(id+"F0.wireOp",EDGE,"E27");var subQ1=sQuery(id+"F0.wireOp",EDGE,"E24");var subQ2=makeQuery(id+"F0.imprint","INTERSECT",VERTEX,{"derivedFrom":[subQ1,subQ0]});Q42=makeQuery(id+"F0.imprint","IMPRINT",FACE,{"disambiguationData":[TD([[makeQuery(id+"F0.imprint","IMPRINT",EDGE,{"disambiguationData":[TD([[subQ2,-1.0]])],"derivedFrom":subQ0}),1.0]])]});}
            var Q43;
            {var subQ0=sQuery(id+"F0.wireOp",EDGE,"E25");var subQ3=sQuery(id+"F0.wireOp",EDGE,"E27");var subQ5=makeQuery(id+"F0.imprint","INTERSECT",VERTEX,{"derivedFrom":[subQ0,subQ3]});Q43=makeQuery(id+"F0.imprint","IMPRINT",FACE,{"disambiguationData":[TD([[makeQuery(id+"F0.imprint","IMPRINT",EDGE,{"disambiguationData":[TD([[subQ5,1.0]])],"derivedFrom":subQ0}),-1.0]])]});}
            var Q44;
            {var subQ0=sQuery(id+"F0.wireOp",EDGE,"E23");var subQ3=sQuery(id+"F0.wireOp",EDGE,"E26");var subQ5=makeQuery(id+"F0.imprint","INTERSECT",VERTEX,{"derivedFrom":[subQ0,subQ3]});Q44=makeQuery(id+"F0.imprint","IMPRINT",FACE,{"disambiguationData":[TD([[makeQuery(id+"F0.imprint","IMPRINT",EDGE,{"disambiguationData":[TD([[subQ5,1.0]])],"derivedFrom":subQ0}),1.0]])]});}
            var Q45;
            {var subQ1=sQuery(id+"F0.wireOp",EDGE,"E24");var subQ3=sQuery(id+"F0.wireOp",EDGE,"E27");var subQ4=makeQuery(id+"F0.imprint","INTERSECT",VERTEX,{"derivedFrom":[subQ1,subQ3]});Q45=makeQuery(id+"F0.imprint","IMPRINT",FACE,{"disambiguationData":[TD([[makeQuery(id+"F0.imprint","IMPRINT",EDGE,{"disambiguationData":[TD([[subQ4,1.0]])],"derivedFrom":subQ3}),1.0]])]});}
            var Q46;
            {var subQ0=sQuery(id+"F0.wireOp",EDGE,"E26");var subQ1=sQuery(id+"F0.wireOp",EDGE,"E23");var subQ2=makeQuery(id+"F0.imprint","INTERSECT",VERTEX,{"derivedFrom":[subQ1,subQ0]});Q46=makeQuery(id+"F0.imprint","IMPRINT",FACE,{"disambiguationData":[TD([[makeQuery(id+"F0.imprint","IMPRINT",EDGE,{"disambiguationData":[TD([[subQ2,-1.0]])],"derivedFrom":subQ1}),1.0]])]});}
            var Q47;
            {var subQ0=sQuery(id+"F0.wireOp",EDGE,"E18");Q47=makeQuery(id+"F0.imprint","IMPRINT",FACE,{"disambiguationData":[TD([[makeQuery(id+"F0.imprint","IMPRINT",EDGE,{"derivedFrom":subQ0}),1.0]])]});}
            var Q48;
            {var subQ1=sQuery(id+"F0.wireOp",EDGE,"E86");var subQ3=sQuery(id+"F0.wireOp",EDGE,"E91");var subQ4=makeQuery(id+"F0.imprint","INTERSECT",VERTEX,{"derivedFrom":[subQ1,subQ3]});Q48=makeQuery(id+"F0.imprint","IMPRINT",FACE,{"disambiguationData":[TD([[makeQuery(id+"F0.imprint","IMPRINT",EDGE,{"disambiguationData":[TD([[subQ4,1.0]])],"derivedFrom":subQ3}),-1.0]])]});}
            var Q49;
            {var subQ0=sQuery(id+"F0.wireOp",EDGE,"E14");var subQ1=sQuery(id+"F0.wireOp",EDGE,"E12");var subQ2=makeQuery(id+"F0.imprint","INTERSECT",VERTEX,{"derivedFrom":[subQ1,subQ0]});Q49=makeQuery(id+"F0.imprint","IMPRINT",FACE,{"disambiguationData":[TD([[makeQuery(id+"F0.imprint","IMPRINT",EDGE,{"disambiguationData":[TD([[subQ2,-1.0]])],"derivedFrom":subQ1}),1.0]])]});}
            var Q50;
            {var subQ0=sQuery(id+"F0.wireOp",EDGE,"E12");var subQ5=sQuery(id+"F0.wireOp",EDGE,"E14");var subQ6=makeQuery(id+"F0.imprint","INTERSECT",VERTEX,{"derivedFrom":[subQ0,subQ5]});Q50=makeQuery(id+"F0.imprint","IMPRINT",FACE,{"disambiguationData":[TD([[makeQuery(id+"F0.imprint","IMPRINT",EDGE,{"disambiguationData":[TD([[subQ6,-1.0]])],"derivedFrom":subQ5}),-1.0]])]});}
            var Q51;
            {var subQ0=sQuery(id+"F0.wireOp",EDGE,"E84");var subQ1=sQuery(id+"F0.wireOp",EDGE,"E10");var subQ2=makeQuery(id+"F0.imprint","INTERSECT",VERTEX,{"derivedFrom":[subQ1,subQ0]});Q51=makeQuery(id+"F0.imprint","IMPRINT",FACE,{"disambiguationData":[TD([[makeQuery(id+"F0.imprint","IMPRINT",EDGE,{"disambiguationData":[TD([[subQ2,-1.0]])],"derivedFrom":subQ1}),1.0]])]});}
            var Q52;
            {var subQ0=sQuery(id+"F0.wireOp",EDGE,"E10");var subQ1=sQuery(id+"F0.wireOp",EDGE,"E7");var subQ2=makeQuery(id+"F0.imprint","INTERSECT",VERTEX,{"derivedFrom":[subQ1,subQ0]});Q52=makeQuery(id+"F0.imprint","IMPRINT",FACE,{"disambiguationData":[TD([[makeQuery(id+"F0.imprint","IMPRINT",EDGE,{"disambiguationData":[TD([[subQ2,-1.0]])],"derivedFrom":subQ1}),1.0]])]});}
            var Q53;
            {var subQ1=sQuery(id+"F0.wireOp",EDGE,"E5");var subQ3=sQuery(id+"F0.wireOp",EDGE,"E81");var subQ4=makeQuery(id+"F0.imprint","INTERSECT",VERTEX,{"derivedFrom":[subQ1,subQ3]});Q53=makeQuery(id+"F0.imprint","IMPRINT",FACE,{"disambiguationData":[TD([[makeQuery(id+"F0.imprint","IMPRINT",EDGE,{"disambiguationData":[TD([[subQ4,-1.0]])],"derivedFrom":subQ3}),1.0]])]});}
            var Q54;
            {var subQ5=sQuery(id+"F0.wireOp",EDGE,"E80");var subQ9=sQuery(id+"F0.wireOp",EDGE,"E1");var subQ10=makeQuery(id+"F0.imprint","INTERSECT",VERTEX,{"derivedFrom":[subQ9,subQ5]});Q54=makeQuery(id+"F0.imprint","IMPRINT",FACE,{"disambiguationData":[TD([[makeQuery(id+"F0.imprint","IMPRINT",EDGE,{"disambiguationData":[TD([[subQ10,-1.0]])],"derivedFrom":subQ9}),-1.0]])]});}
            var Q55;
            {var subQ1=sQuery(id+"F0.wireOp",EDGE,"E69");var subQ5=sQuery(id+"F0.wireOp",EDGE,"E3");var subQ6=makeQuery(id+"F0.imprint","INTERSECT",VERTEX,{"derivedFrom":[subQ5,subQ1]});Q55=makeQuery(id+"F0.imprint","IMPRINT",FACE,{"disambiguationData":[TD([[makeQuery(id+"F0.imprint","IMPRINT",EDGE,{"disambiguationData":[TD([[subQ6,-1.0]])],"derivedFrom":subQ5}),1.0]])]});}
            var Q56;
            {var subQ0=sQuery(id+"F0.wireOp",EDGE,"E70");var subQ5=sQuery(id+"F0.wireOp",EDGE,"E77");var subQ6=makeQuery(id+"F0.imprint","INTERSECT",VERTEX,{"derivedFrom":[subQ0,subQ5]});Q56=makeQuery(id+"F0.imprint","IMPRINT",FACE,{"disambiguationData":[TD([[makeQuery(id+"F0.imprint","IMPRINT",EDGE,{"disambiguationData":[TD([[subQ6,-1.0]])],"derivedFrom":subQ5}),1.0]])]});}
            var Q57;
            {var subQ0=sQuery(id+"F0.wireOp",EDGE,"E59");var subQ5=sQuery(id+"F0.wireOp",EDGE,"E62");var subQ6=makeQuery(id+"F0.imprint","INTERSECT",VERTEX,{"derivedFrom":[subQ0,subQ5]});Q57=makeQuery(id+"F0.imprint","IMPRINT",FACE,{"disambiguationData":[TD([[makeQuery(id+"F0.imprint","IMPRINT",EDGE,{"disambiguationData":[TD([[subQ6,-1.0]])],"derivedFrom":subQ5}),1.0]])]});}
            var Q58;
            {var subQ1=sQuery(id+"F0.wireOp",EDGE,"E58");var subQ3=sQuery(id+"F0.wireOp",EDGE,"E60");var subQ4=makeQuery(id+"F0.imprint","INTERSECT",VERTEX,{"derivedFrom":[subQ1,subQ3]});Q58=makeQuery(id+"F0.imprint","IMPRINT",FACE,{"disambiguationData":[TD([[makeQuery(id+"F0.imprint","IMPRINT",EDGE,{"disambiguationData":[TD([[subQ4,1.0]])],"derivedFrom":subQ3}),-1.0]])]});}
            var Q59;
            {var subQ1=sQuery(id+"F0.wireOp",EDGE,"E67");var subQ5=sQuery(id+"F0.wireOp",EDGE,"E62");var subQ7=makeQuery(id+"F0.imprint","INTERSECT",VERTEX,{"derivedFrom":[subQ5,subQ1]});Q59=makeQuery(id+"F0.imprint","IMPRINT",FACE,{"disambiguationData":[TD([[makeQuery(id+"F0.imprint","IMPRINT",EDGE,{"disambiguationData":[TD([[subQ7,-1.0]])],"derivedFrom":subQ5}),1.0]])]});}
            var Q60;
            {var subQ0=sQuery(id+"F0.wireOp",EDGE,"E68");var subQ1=sQuery(id+"F0.wireOp",EDGE,"E1");var subQ3=makeQuery(id+"F0.imprint","INTERSECT",VERTEX,{"derivedFrom":[subQ1,subQ0]});Q60=makeQuery(id+"F0.imprint","IMPRINT",FACE,{"disambiguationData":[TD([[makeQuery(id+"F0.imprint","IMPRINT",EDGE,{"disambiguationData":[TD([[subQ3,1.0]])],"derivedFrom":subQ1}),1.0]])]});}
            var Q61;
            {var subQ3=sQuery(id+"F0.wireOp",EDGE,"E67");var subQ7=sQuery(id+"F0.wireOp",EDGE,"E62");var subQ8=makeQuery(id+"F0.imprint","INTERSECT",VERTEX,{"derivedFrom":[subQ7,subQ3]});Q61=makeQuery(id+"F0.imprint","IMPRINT",FACE,{"disambiguationData":[TD([[makeQuery(id+"F0.imprint","IMPRINT",EDGE,{"disambiguationData":[TD([[subQ8,-1.0]])],"derivedFrom":subQ7}),-1.0]])]});}
            var Q62;
            {var subQ0=sQuery(id+"F0.wireOp",EDGE,"E68");var subQ1=sQuery(id+"F0.wireOp",EDGE,"E63");var subQ2=makeQuery(id+"F0.imprint","INTERSECT",VERTEX,{"derivedFrom":[subQ1,subQ0]});Q62=makeQuery(id+"F0.imprint","IMPRINT",FACE,{"disambiguationData":[TD([[makeQuery(id+"F0.imprint","IMPRINT",EDGE,{"disambiguationData":[TD([[subQ2,-1.0]])],"derivedFrom":subQ1}),1.0]])]});}
            var Q63;
            {var subQ1=sQuery(id+"F0.wireOp",EDGE,"E65");var subQ3=sQuery(id+"F0.wireOp",EDGE,"E68");var subQ4=makeQuery(id+"F0.imprint","INTERSECT",VERTEX,{"derivedFrom":[subQ1,subQ3]});Q63=makeQuery(id+"F0.imprint","IMPRINT",FACE,{"disambiguationData":[TD([[makeQuery(id+"F0.imprint","IMPRINT",EDGE,{"disambiguationData":[TD([[subQ4,-1.0]])],"derivedFrom":subQ3}),1.0]])]});}
            var Q64;
            {var subQ0=sQuery(id+"F0.wireOp",EDGE,"E74");var subQ1=sQuery(id+"F0.wireOp",EDGE,"E68");var subQ2=makeQuery(id+"F0.imprint","INTERSECT",VERTEX,{"derivedFrom":[subQ1,subQ0]});Q64=makeQuery(id+"F0.imprint","IMPRINT",FACE,{"disambiguationData":[TD([[makeQuery(id+"F0.imprint","IMPRINT",EDGE,{"disambiguationData":[TD([[subQ2,-1.0]])],"derivedFrom":subQ1}),1.0]])]});}
            var Q65;
            {var subQ0=sQuery(id+"F0.wireOp",EDGE,"E46");var subQ1=sQuery(id+"F0.wireOp",EDGE,"E44");var subQ2=makeQuery(id+"F0.imprint","INTERSECT",VERTEX,{"derivedFrom":[subQ1,subQ0]});Q65=makeQuery(id+"F0.imprint","IMPRINT",FACE,{"disambiguationData":[TD([[makeQuery(id+"F0.imprint","IMPRINT",EDGE,{"disambiguationData":[TD([[subQ2,-1.0]])],"derivedFrom":subQ1}),1.0]])]});}
            var Q66;
            {var subQ1=sQuery(id+"F0.wireOp",EDGE,"E45");var subQ3=sQuery(id+"F0.wireOp",EDGE,"E47");var subQ4=makeQuery(id+"F0.imprint","INTERSECT",VERTEX,{"derivedFrom":[subQ1,subQ3]});Q66=makeQuery(id+"F0.imprint","IMPRINT",FACE,{"disambiguationData":[TD([[makeQuery(id+"F0.imprint","IMPRINT",EDGE,{"disambiguationData":[TD([[subQ4,-1.0]])],"derivedFrom":subQ3}),1.0]])]});}
            var Q67;
            {var subQ0=sQuery(id+"F0.wireOp",EDGE,"E52");var subQ1=sQuery(id+"F0.wireOp",EDGE,"E49");var subQ2=makeQuery(id+"F0.imprint","INTERSECT",VERTEX,{"derivedFrom":[subQ1,subQ0]});Q67=makeQuery(id+"F0.imprint","IMPRINT",FACE,{"disambiguationData":[TD([[makeQuery(id+"F0.imprint","IMPRINT",EDGE,{"disambiguationData":[TD([[subQ2,-1.0]])],"derivedFrom":subQ1}),-1.0]])]});}
            var Q68;
            {var subQ0=sQuery(id+"F0.wireOp",EDGE,"E57");var subQ1=sQuery(id+"F0.wireOp",EDGE,"E54");var subQ2=makeQuery(id+"F0.imprint","INTERSECT",VERTEX,{"derivedFrom":[subQ1,subQ0]});Q68=makeQuery(id+"F0.imprint","IMPRINT",FACE,{"disambiguationData":[TD([[makeQuery(id+"F0.imprint","IMPRINT",EDGE,{"disambiguationData":[TD([[subQ2,-1.0]])],"derivedFrom":subQ1}),1.0]])]});}
            var Q69;
            {var subQ0=sQuery(id+"F0.wireOp",EDGE,"E90");var subQ1=sQuery(id+"F0.wireOp",EDGE,"E16");var subQ2=makeQuery(id+"F0.imprint","INTERSECT",VERTEX,{"derivedFrom":[subQ1,subQ0]});Q69=makeQuery(id+"F0.imprint","IMPRINT",FACE,{"disambiguationData":[TD([[makeQuery(id+"F0.imprint","IMPRINT",EDGE,{"disambiguationData":[TD([[subQ2,-1.0]])],"derivedFrom":subQ1}),1.0]])]});}
            var Q70;
            {var subQ1=sQuery(id+"F0.wireOp",EDGE,"E16");var subQ3=sQuery(id+"F0.wireOp",EDGE,"E89");var subQ4=makeQuery(id+"F0.imprint","INTERSECT",VERTEX,{"derivedFrom":[subQ1,subQ3]});Q70=makeQuery(id+"F0.imprint","IMPRINT",FACE,{"disambiguationData":[TD([[makeQuery(id+"F0.imprint","IMPRINT",EDGE,{"disambiguationData":[TD([[subQ4,-1.0]])],"derivedFrom":subQ1}),-1.0]])]});}
            var Q71;
            {var subQ0=sQuery(id+"F0.wireOp",EDGE,"E18");Q71=makeQuery(id+"F0.imprint","IMPRINT",FACE,{"disambiguationData":[TD([[makeQuery(id+"F0.imprint","IMPRINT",EDGE,{"derivedFrom":subQ0}),-1.0]])]});}
            var Q72;
            {var subQ1=sQuery(id+"F0.wireOp",EDGE,"E0");var subQ7=sQuery(id+"F0.wireOp",EDGE,"E94");var subQ8=makeQuery(id+"F0.imprint","INTERSECT",VERTEX,{"derivedFrom":[subQ1,subQ7]});Q72=makeQuery(id+"F0.imprint","IMPRINT",FACE,{"disambiguationData":[TD([[makeQuery(id+"F0.imprint","IMPRINT",EDGE,{"disambiguationData":[TD([[subQ8,-1.0]])],"derivedFrom":subQ7}),-1.0]])]});}
            var Q73;
            {var subQ1=sQuery(id+"F0.wireOp",EDGE,"E10");var subQ5=sQuery(id+"F0.wireOp",EDGE,"E85");var subQ6=makeQuery(id+"F0.imprint","INTERSECT",VERTEX,{"derivedFrom":[subQ1,subQ5]});Q73=makeQuery(id+"F0.imprint","IMPRINT",FACE,{"disambiguationData":[TD([[makeQuery(id+"F0.imprint","IMPRINT",EDGE,{"disambiguationData":[TD([[subQ6,-1.0]])],"derivedFrom":subQ1}),1.0]])]});}
            var Q74;
            {var subQ1=sQuery(id+"F0.wireOp",EDGE,"E13");var subQ3=sQuery(id+"F0.wireOp",EDGE,"E86");var subQ4=makeQuery(id+"F0.imprint","INTERSECT",VERTEX,{"derivedFrom":[subQ1,subQ3]});Q74=makeQuery(id+"F0.imprint","IMPRINT",FACE,{"disambiguationData":[TD([[makeQuery(id+"F0.imprint","IMPRINT",EDGE,{"disambiguationData":[TD([[subQ4,-1.0]])],"derivedFrom":subQ3}),1.0]])]});}
            var Q75;
            {var subQ1=sQuery(id+"F0.wireOp",EDGE,"E34");var subQ3=sQuery(id+"F0.wireOp",EDGE,"E42");var subQ4=makeQuery(id+"F0.imprint","INTERSECT",VERTEX,{"derivedFrom":[subQ1,subQ3]});Q75=makeQuery(id+"F0.imprint","IMPRINT",FACE,{"disambiguationData":[TD([[makeQuery(id+"F0.imprint","IMPRINT",EDGE,{"disambiguationData":[TD([[subQ4,-1.0]])],"derivedFrom":subQ3}),-1.0]])]});}
            var Q76;
            {var subQ1=sQuery(id+"F0.wireOp",EDGE,"E38");var subQ3=sQuery(id+"F0.wireOp",EDGE,"E42");var subQ4=makeQuery(id+"F0.imprint","INTERSECT",VERTEX,{"derivedFrom":[subQ1,subQ3]});Q76=makeQuery(id+"F0.imprint","IMPRINT",FACE,{"disambiguationData":[TD([[makeQuery(id+"F0.imprint","IMPRINT",EDGE,{"disambiguationData":[TD([[subQ4,-1.0]])],"derivedFrom":subQ1}),-1.0]])]});}
            extrude(context, id + "F1", {"entities" : qUnion([Q0, Q1, Q2, Q3, Q4, Q5, Q6, Q7, Q8, Q9, Q10, Q11, Q12, Q13, Q14, Q15, Q16, Q17, Q18, Q19, Q20, Q21, Q22, Q23, Q24, Q25, Q26, Q27, Q28, Q29, Q30, Q31, Q32, Q33, Q34, Q35, Q36, Q37, Q38, Q39, Q40, Q41, Q42, Q43, Q44, Q45, Q46, Q47, Q48, Q49, Q50, Q51, Q52, Q53, Q54, Q55, Q56, Q57, Q58, Q59, Q60, Q61, Q62, Q63, Q64, Q65, Q66, Q67, Q68, Q69, Q70, Q71, Q72, Q73, Q74, Q75, Q76]), "depth" : 34.04 * mm});
        }
        {
            var Q0;
            {var subQ4=sQuery(id+"F0.wireOp",EDGE,"E43");Q0=makeQuery(id+"F0.imprint","IMPRINT",FACE,{"disambiguationData":[TD([[makeQuery(id+"F0.imprint","IMPRINT",EDGE,{"derivedFrom":subQ4}),1.0]])]});}
            extrude(context, id + "F2", {"entities" : qUnion([Q0]), "depth" : 2.54 * mm});
        }
        {
            var Q0;
            Q0=makeQuery(id+"F1.opExtrude","CAP_FACE",FACE,{"disambiguationData":[OSD([sQuery(id+"F0.wireOp",EDGE,"E0"),sQuery(id+"F0.wireOp",EDGE,"E1"),sQuery(id+"F0.wireOp",EDGE,"E8"),sQuery(id+"F0.wireOp",EDGE,"E10"),sQuery(id+"F0.wireOp",EDGE,"E11"),sQuery(id+"F0.wireOp",EDGE,"E12"),sQuery(id+"F0.wireOp",EDGE,"E14"),sQuery(id+"F0.wireOp",EDGE,"E15"),sQuery(id+"F0.wireOp",EDGE,"E16"),sQuery(id+"F0.wireOp",EDGE,"E17"),sQuery(id+"F0.wireOp",EDGE,"E19"),sQuery(id+"F0.wireOp",EDGE,"E21"),sQuery(id+"F0.wireOp",EDGE,"E22"),sQuery(id+"F0.wireOp",EDGE,"E23"),sQuery(id+"F0.wireOp",EDGE,"E25"),sQuery(id+"F0.wireOp",EDGE,"E26"),sQuery(id+"F0.wireOp",EDGE,"E27"),sQuery(id+"F0.wireOp",EDGE,"E29"),sQuery(id+"F0.wireOp",EDGE,"E30"),sQuery(id+"F0.wireOp",EDGE,"E35"),sQuery(id+"F0.wireOp",EDGE,"E36"),sQuery(id+"F0.wireOp",EDGE,"E37"),sQuery(id+"F0.wireOp",EDGE,"E41"),sQuery(id+"F0.wireOp",EDGE,"E42"),sQuery(id+"F0.wireOp",EDGE,"E44"),sQuery(id+"F0.wireOp",EDGE,"E47"),sQuery(id+"F0.wireOp",EDGE,"E49"),sQuery(id+"F0.wireOp",EDGE,"E50"),sQuery(id+"F0.wireOp",EDGE,"E51"),sQuery(id+"F0.wireOp",EDGE,"E52"),sQuery(id+"F0.wireOp",EDGE,"E54"),sQuery(id+"F0.wireOp",EDGE,"E55"),sQuery(id+"F0.wireOp",EDGE,"E58"),sQuery(id+"F0.wireOp",EDGE,"E60"),sQuery(id+"F0.wireOp",EDGE,"E62"),sQuery(id+"F0.wireOp",EDGE,"E63"),sQuery(id+"F0.wireOp",EDGE,"E65"),sQuery(id+"F0.wireOp",EDGE,"E67"),sQuery(id+"F0.wireOp",EDGE,"E68"),sQuery(id+"F0.wireOp",EDGE,"E72"),sQuery(id+"F0.wireOp",EDGE,"E75"),sQuery(id+"F0.wireOp",EDGE,"E86"),sQuery(id+"F0.wireOp",EDGE,"E89"),sQuery(id+"F0.wireOp",EDGE,"E91"),sQuery(id+"F0.wireOp",EDGE,"E92"),sQuery(id+"F0.wireOp",EDGE,"E93"),sQuery(id+"F0.wireOp",EDGE,"E94")])],"isStart":false});
            var Q1;
            Q1=makeQuery(id+"F1.opExtrude","CAP_FACE",FACE,{"disambiguationData":[OSD([sQuery(id+"F0.wireOp",EDGE,"E1"),sQuery(id+"F0.wireOp",EDGE,"E3"),sQuery(id+"F0.wireOp",EDGE,"E4"),sQuery(id+"F0.wireOp",EDGE,"E5"),sQuery(id+"F0.wireOp",EDGE,"E7"),sQuery(id+"F0.wireOp",EDGE,"E10"),sQuery(id+"F0.wireOp",EDGE,"E69"),sQuery(id+"F0.wireOp",EDGE,"E71"),sQuery(id+"F0.wireOp",EDGE,"E76"),sQuery(id+"F0.wireOp",EDGE,"E77"),sQuery(id+"F0.wireOp",EDGE,"E80"),sQuery(id+"F0.wireOp",EDGE,"E81")])],"isStart":false});
            var Q2;
            Q2=makeQuery(id+"F1.opExtrude","CAP_FACE",FACE,{"disambiguationData":[OSD([sQuery(id+"F0.wireOp",EDGE,"E1"),sQuery(id+"F0.wireOp",EDGE,"E71"),sQuery(id+"F0.wireOp",EDGE,"E75")])],"isStart":false});
            extrude(context, id + "F3", {"entities" : qUnion([Q0, Q1, Q2]), "depth" : 27.7 * mm});
        }
        {
            var Q0;
            Q0=makeQuery(id+"F3.opExtrude","SWEPT_FACE",FACE,{"disambiguationData":[OSD([sQuery(id+"F0.wireOp",EDGE,"E54")])]});
            var sketch = newSketch(context, id + "F4", { "sketchPlane" : qUnion([Q0])});
            skCircle(sketch, "E95", {"center": v(-9.2, 50.5) * mm, "radius": 4.1 * mm});
            skCircle(sketch, "E96", {"center": v(-9.2, 14.85) * mm, "radius": 4 * mm});
            skSolve(sketch);
        }
        {
            var Q0;
            Q0 = qSketchRegion(id + "F4", true);
            extrude(context, id + "F5", {"entities" : qUnion([Q0]), "depth" : 27.43 * mm});
        }
        {
            var Q0;
            Q0=makeQuery(id+"F5.opExtrude","CAP_FACE",FACE,{"disambiguationData":[OSD([sQuery(id+"F4.wireOp",EDGE,"E95")])],"isStart":false});
            var sketch = newSketch(context, id + "F6", { "sketchPlane" : qUnion([Q0])});
            skFitSpline(sketch, "E97", {"points": [v(-9.05, 54.58) * mm, v(-17.43, 31.83) * mm, v(-9.97, 11.26) * mm, v(0, 31.83) * mm, v(-9.05, 54.58) * mm]});
            skSolve(sketch);
        }
        {
            var Q0;
            Q0 = qSketchRegion(id + "F6", true);
            extrude(context, id + "F7", {"entities" : qUnion([Q0]), "oppositeDirection" : true, "depth" : 2.54 * mm});
        }
    });
